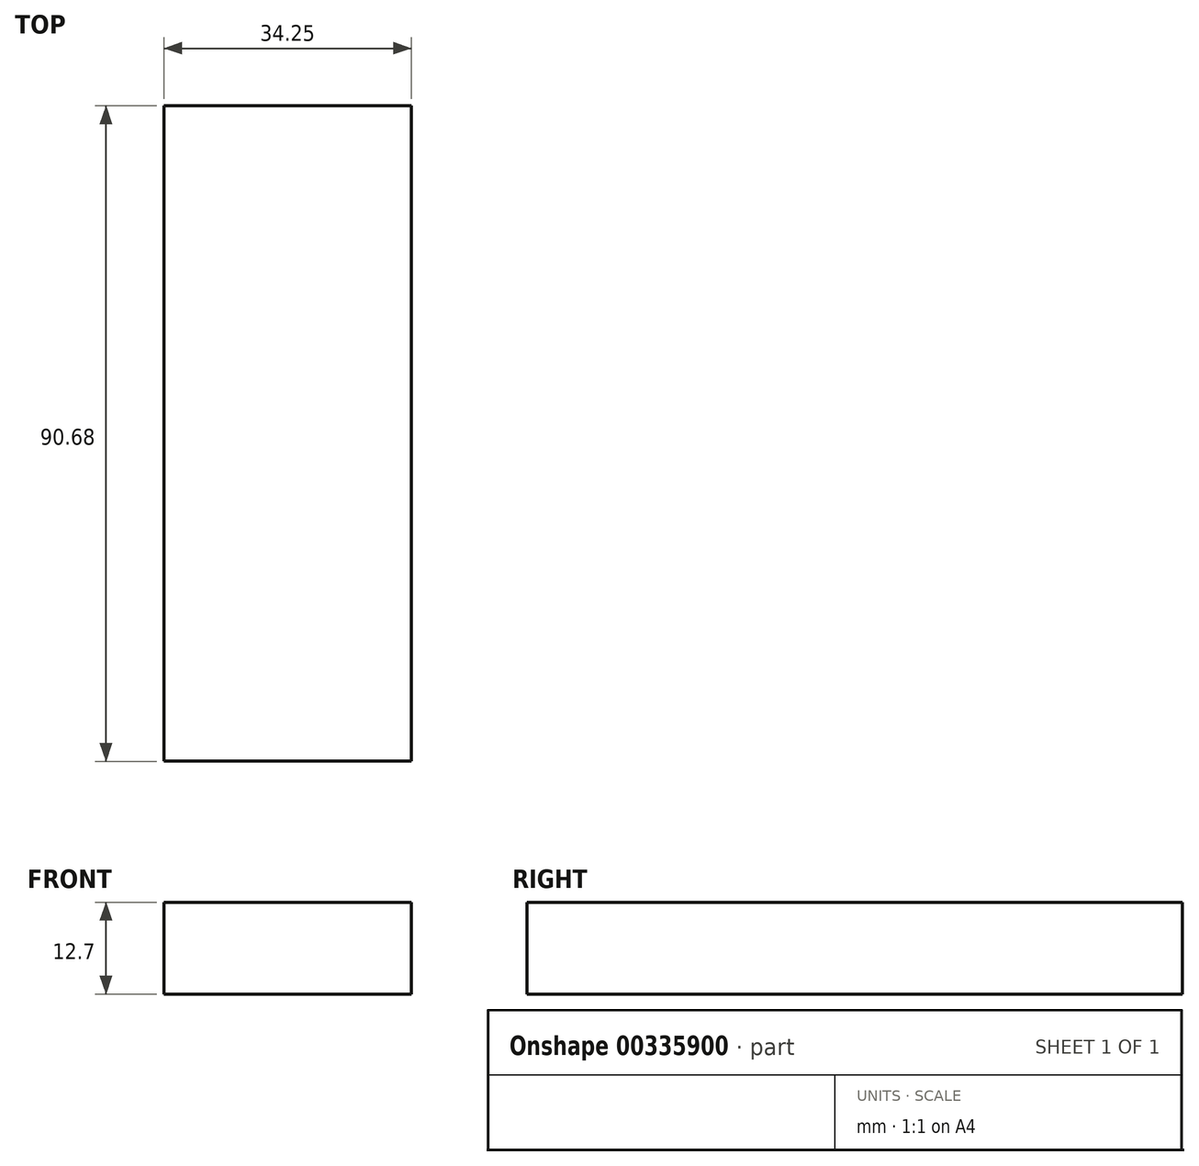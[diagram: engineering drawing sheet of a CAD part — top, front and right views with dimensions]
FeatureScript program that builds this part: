
annotation { "Feature Type Name" : "Feature", "Feature Type Description" : "" }
export const myFeature = defineFeature(function(context is Context, id is Id, definition is map)
    precondition{}
    {
        {
            var Q0;
            Q0=qCreatedBy(makeId("Front.planeOp"),FACE);
            var sketch = newSketch(context, id + "F0", { "sketchPlane" : qUnion([Q0])});
            skLineSegment(sketch, "E0.bottom", {"start": v(0, 0) * mm, "end": v(-34.25, 0) * mm});
            skLineSegment(sketch, "E0.top", {"start": v(0, 12.7) * mm, "end": v(-34.25, 12.7) * mm});
            skLineSegment(sketch, "E0.left", {"start": v(0, 0) * mm, "end": v(0, 12.7) * mm});
            skLineSegment(sketch, "E0.right", {"start": v(-34.25, 0) * mm, "end": v(-34.25, 12.7) * mm});
            skLineSegment(sketch, "E1.bottom", {"start": v(-34.25, 12.7) * mm, "end": v(-29.25, 12.7) * mm});
            skLineSegment(sketch, "E1.top", {"start": v(-34.25, 12.7) * mm, "end": v(-29.25, 12.7) * mm});
            skLineSegment(sketch, "E1.left", {"start": v(-34.25, 12.7) * mm, "end": v(-34.25, 12.7) * mm});
            skLineSegment(sketch, "E1.right", {"start": v(-29.25, 12.7) * mm, "end": v(-29.25, 12.7) * mm});
            skSolve(sketch);
        }
        {
            var Q0;
            Q0=makeQuery(id+"F0.imprint","IMPRINT",FACE,{"disambiguationData":[TD([[makeQuery(id+"F0.imprint","IMPRINT",EDGE,{"derivedFrom":sQuery(id+"F0.wireOp",EDGE,"E0.bottom")}),-1.0]])]});
            extrude(context, id + "F1", {"entities" : qUnion([Q0]), "depth" : 90.68 * mm});
        }
    });
